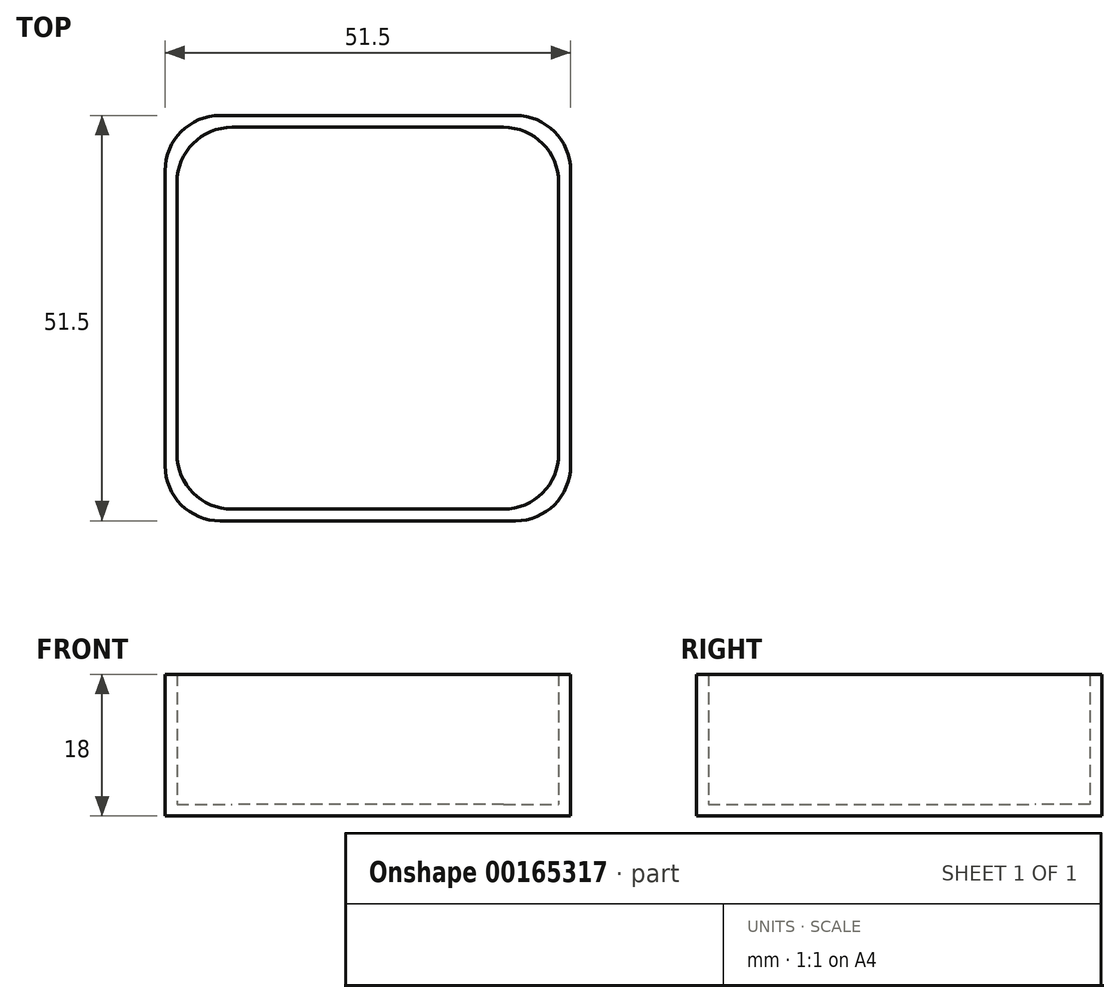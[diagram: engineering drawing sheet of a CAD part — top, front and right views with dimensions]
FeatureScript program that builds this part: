
annotation { "Feature Type Name" : "Feature", "Feature Type Description" : "" }
export const myFeature = defineFeature(function(context is Context, id is Id, definition is map)
    precondition{}
    {
        {
            var Q0;
            Q0=qCreatedBy(makeId("Top.planeOp"),FACE);
            var sketch = newSketch(context, id + "F0", { "sketchPlane" : qUnion([Q0])});
            skLineSegment(sketch, "E0.bottom", {"start": v(-33.74, 27.93) * mm, "end": v(3.76, 27.93) * mm});
            skLineSegment(sketch, "E0.top", {"start": v(-33.74, -23.57) * mm, "end": v(3.76, -23.57) * mm});
            skLineSegment(sketch, "E0.left", {"start": v(-40.74, 20.93) * mm, "end": v(-40.74, -16.57) * mm});
            skLineSegment(sketch, "E0.right", {"start": v(10.76, 20.93) * mm, "end": v(10.76, -16.57) * mm});
            skPoint(sketch, "E1.visualSharp", {"position": v(-40.74, 27.93) * mm});
            skArc(sketch, "E1.filletArc", {"start": v(-33.74, 27.93) * mm, "mid": v(-38.69, 25.88) * mm, "end": v(-40.74, 20.93) * mm});
            skPoint(sketch, "E2.visualSharp", {"position": v(10.76, 27.93) * mm});
            skArc(sketch, "E2.filletArc", {"start": v(10.76, 20.93) * mm, "mid": v(8.71, 25.88) * mm, "end": v(3.76, 27.93) * mm});
            skPoint(sketch, "E3.visualSharp", {"position": v(10.76, -23.57) * mm});
            skArc(sketch, "E3.filletArc", {"start": v(3.76, -23.57) * mm, "mid": v(8.71, -21.52) * mm, "end": v(10.76, -16.57) * mm});
            skPoint(sketch, "E4.visualSharp", {"position": v(-40.74, -23.57) * mm});
            skArc(sketch, "E4.filletArc", {"start": v(-40.74, -16.57) * mm, "mid": v(-38.69, -21.52) * mm, "end": v(-33.74, -23.57) * mm});
            skSolve(sketch);
        }
        {
            var Q0;
            Q0=makeQuery(id+"F0.imprint","IMPRINT",FACE,{"disambiguationData":[TD([[makeQuery(id+"F0.imprint","IMPRINT",EDGE,{"derivedFrom":sQuery(id+"F0.wireOp",EDGE,"E0.bottom")}),-1.0]])]});
            extrude(context, id + "F1", {"entities" : qUnion([Q0]), "depth" : 1.5 * mm});
        }
        {
            var Q0;
            Q0=makeQuery(id+"F1.opExtrude","CAP_FACE",FACE,{"disambiguationData":[OSD([sQuery(id+"F0.wireOp",EDGE,"E0.bottom"),sQuery(id+"F0.wireOp",EDGE,"E0.top"),sQuery(id+"F0.wireOp",EDGE,"E0.left"),sQuery(id+"F0.wireOp",EDGE,"E0.right"),sQuery(id+"F0.wireOp",EDGE,"E1.filletArc"),sQuery(id+"F0.wireOp",EDGE,"E2.filletArc"),sQuery(id+"F0.wireOp",EDGE,"E3.filletArc"),sQuery(id+"F0.wireOp",EDGE,"E4.filletArc")])],"isStart":false});
            var sketch = newSketch(context, id + "F2", { "sketchPlane" : qUnion([Q0])});
            skLineSegment(sketch, "E5.bottom", {"start": v(2.26, -22.07) * mm, "end": v(-32.24, -22.07) * mm});
            skLineSegment(sketch, "E5.top", {"start": v(2.26, 26.43) * mm, "end": v(-32.24, 26.43) * mm});
            skLineSegment(sketch, "E5.left", {"start": v(9.26, -15.07) * mm, "end": v(9.26, 19.43) * mm});
            skLineSegment(sketch, "E5.right", {"start": v(-39.24, -15.07) * mm, "end": v(-39.24, 19.43) * mm});
            skLineSegment(sketch, "E6", {"start": v(-14.8, -22.07) * mm, "end": v(-14.8, -23.57) * mm});
            skLineSegment(sketch, "E7", {"start": v(-14.99, 26.43) * mm, "end": v(-14.99, 27.93) * mm});
            skLineSegment(sketch, "E8", {"start": v(-39.24, 2.18) * mm, "end": v(-40.74, 2.18) * mm});
            skLineSegment(sketch, "E9", {"start": v(9.26, 0) * mm, "end": v(10.76, 0) * mm});
            skPoint(sketch, "E10.visualSharp", {"position": v(9.26, -22.07) * mm});
            skArc(sketch, "E10.filletArc", {"start": v(2.26, -22.07) * mm, "mid": v(7.21, -20.02) * mm, "end": v(9.26, -15.07) * mm});
            skPoint(sketch, "E11.visualSharp", {"position": v(-39.24, -22.07) * mm});
            skArc(sketch, "E11.filletArc", {"start": v(-39.24, -15.07) * mm, "mid": v(-37.19, -20.02) * mm, "end": v(-32.24, -22.07) * mm});
            skPoint(sketch, "E12.visualSharp", {"position": v(-39.24, 26.43) * mm});
            skArc(sketch, "E12.filletArc", {"start": v(-32.24, 26.43) * mm, "mid": v(-37.19, 24.38) * mm, "end": v(-39.24, 19.43) * mm});
            skPoint(sketch, "E13.visualSharp", {"position": v(9.26, 26.43) * mm});
            skArc(sketch, "E13.filletArc", {"start": v(9.26, 19.43) * mm, "mid": v(7.21, 24.38) * mm, "end": v(2.26, 26.43) * mm});
            skLineSegment(sketch, "E14.bottom", {"start": v(-33.29, 20.48) * mm, "end": v(3.31, 20.48) * mm});
            skLineSegment(sketch, "E14.top", {"start": v(-33.29, -16.12) * mm, "end": v(3.31, -16.12) * mm});
            skLineSegment(sketch, "E14.left", {"start": v(-33.29, 20.48) * mm, "end": v(-33.29, -16.12) * mm});
            skLineSegment(sketch, "E14.right", {"start": v(3.31, 20.48) * mm, "end": v(3.31, -16.12) * mm});
            skLineSegment(sketch, "E15", {"start": v(-14.99, 26.43) * mm, "end": v(-14.99, 20.48) * mm});
            skLineSegment(sketch, "E16", {"start": v(-39.24, 2.18) * mm, "end": v(-33.29, 2.18) * mm});
            skLineSegment(sketch, "E17", {"start": v(-14.8, -22.07) * mm, "end": v(-14.8, -16.12) * mm});
            skLineSegment(sketch, "E18", {"start": v(9.26, 0) * mm, "end": v(3.31, 0) * mm});
            skSolve(sketch);
        }
        {
            var Q0;
            {var subQ5=sQuery(id+"F2.wireOp",EDGE,"E6");Q0=makeQuery(id+"F2.imprint","IMPRINT",FACE,{"disambiguationData":[TD([[makeQuery(id+"F2.imprint","IMPRINT",EDGE,{"derivedFrom":subQ5}),1.0]])]});}
            var Q1;
            {var subQ3=sQuery(id+"F2.wireOp",EDGE,"E6");Q1=makeQuery(id+"F2.imprint","IMPRINT",FACE,{"disambiguationData":[TD([[makeQuery(id+"F2.imprint","IMPRINT",EDGE,{"derivedFrom":subQ3}),-1.0]])]});}
            var Q2;
            {var subQ4=sQuery(id+"F2.wireOp",EDGE,"E7");Q2=makeQuery(id+"F2.imprint","IMPRINT",FACE,{"disambiguationData":[TD([[makeQuery(id+"F2.imprint","IMPRINT",EDGE,{"derivedFrom":subQ4}),1.0]])]});}
            var Q3;
            {var subQ3=sQuery(id+"F2.wireOp",EDGE,"E7");Q3=makeQuery(id+"F2.imprint","IMPRINT",FACE,{"disambiguationData":[TD([[makeQuery(id+"F2.imprint","IMPRINT",EDGE,{"derivedFrom":subQ3}),-1.0]])]});}
            extrude(context, id + "F3", {"entities" : qUnion([Q0, Q1, Q2, Q3]), "operationType" : NewBodyOperationType.ADD, "depth" : 16.5 * mm});
        }
    });
